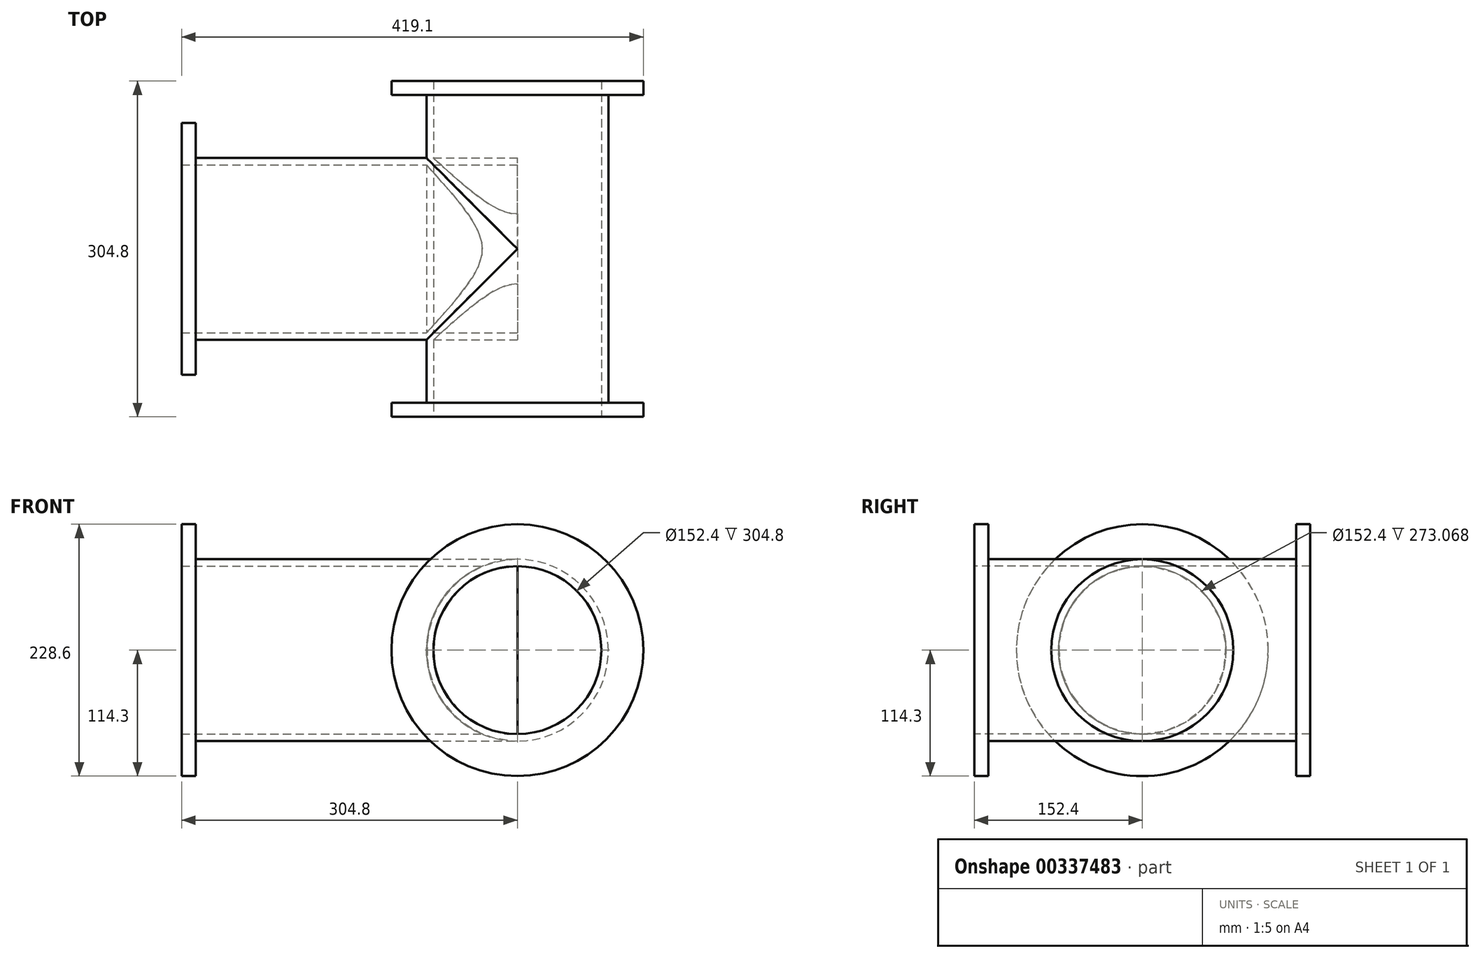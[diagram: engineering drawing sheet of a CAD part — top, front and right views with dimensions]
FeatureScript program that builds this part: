
annotation { "Feature Type Name" : "Feature", "Feature Type Description" : "" }
export const myFeature = defineFeature(function(context is Context, id is Id, definition is map)
    precondition{}
    {
        {
            var Q0;
            Q0=qCreatedBy(makeId("Right.planeOp"),FACE);
            var sketch = newSketch(context, id + "F0", { "sketchPlane" : qUnion([Q0])});
            skLineSegment(sketch, "E0", {"start": v(-372.41, 0) * mm, "end": v(512.39, 0) * mm, "construction": true});
            skLineSegment(sketch, "E1", {"start": v(0, 114.3) * mm, "end": v(-12.7, 114.3) * mm});
            skLineSegment(sketch, "E2", {"start": v(-12.7, 114.3) * mm, "end": v(-12.7, 82.55) * mm});
            skLineSegment(sketch, "E3", {"start": v(-12.7, 82.55) * mm, "end": v(-292.1, 82.55) * mm});
            skLineSegment(sketch, "E4", {"start": v(-292.1, 82.55) * mm, "end": v(-292.1, 114.3) * mm});
            skLineSegment(sketch, "E5", {"start": v(-292.1, 114.3) * mm, "end": v(-304.8, 114.3) * mm});
            skLineSegment(sketch, "E6", {"start": v(-304.8, 76.2) * mm, "end": v(0, 76.2) * mm});
            skLineSegment(sketch, "E7", {"start": v(-304.8, 114.3) * mm, "end": v(-304.8, 76.2) * mm});
            skLineSegment(sketch, "E8", {"start": v(0, 114.3) * mm, "end": v(0, 76.2) * mm});
            skSolve(sketch);
        }
        {
            var Q0;
            Q0=makeQuery(id+"F0.imprint","IMPRINT",FACE,{"disambiguationData":[TD([[makeQuery(id+"F0.imprint","IMPRINT",EDGE,{"derivedFrom":sQuery(id+"F0.wireOp",EDGE,"E1")}),1.0]])]});
            var Q1;
            Q1=sQuery(id+"F0.wireOp",EDGE,"E0");
            revolve(context, id + "F1", {"entities" : qUnion([Q0]), "axis" : qUnion([Q1]), "revolveType" : RevolveType.FULL});
        }
        {
            var Q0;
            Q0=makeQuery(id+"F1.opRevolve","SWEPT_FACE",FACE,{"disambiguationData":[OSD([sQuery(id+"F0.wireOp",EDGE,"E8")])]});
            var Q1;
            Q1=makeQuery(id+"F1.opRevolve","SWEPT_FACE",FACE,{"disambiguationData":[OSD([sQuery(id+"F0.wireOp",EDGE,"E7")])]});
            cPlane(context, id + "F2", {"entities" : qUnion([Q0, Q1]), "cplaneType" : CPlaneType.MID_PLANE, "offset" : 25.4 * mm, "width" : 152.4 * mm, "height" : 152.4 * mm});
        }
        {
            var Q0;
            Q0=qCreatedBy(id+"F2.planeOp",FACE);
            var sketch = newSketch(context, id + "F3", { "sketchPlane" : qUnion([Q0])});
            skLineSegment(sketch, "E9", {"start": v(304.8, 114.3) * mm, "end": v(292.1, 114.3) * mm});
            skLineSegment(sketch, "E10", {"start": v(292.1, 114.3) * mm, "end": v(292.1, 82.55) * mm});
            skLineSegment(sketch, "E11", {"start": v(292.1, 82.55) * mm, "end": v(0, 82.55) * mm});
            skLineSegment(sketch, "E12", {"start": v(0, 76.2) * mm, "end": v(304.8, 76.2) * mm});
            skLineSegment(sketch, "E13", {"start": v(304.8, 114.3) * mm, "end": v(304.8, 76.2) * mm});
            skLineSegment(sketch, "E14", {"start": v(0, 82.55) * mm, "end": v(0, 76.2) * mm});
            skLineSegment(sketch, "E15", {"start": v(328.87, 0) * mm, "end": v(-308.32, 0) * mm, "construction": true});
            skSolve(sketch);
        }
        {
            var Q0;
            Q0=makeQuery(id+"F3.imprint","IMPRINT",FACE,{"disambiguationData":[TD([[makeQuery(id+"F3.imprint","IMPRINT",EDGE,{"derivedFrom":sQuery(id+"F3.wireOp",EDGE,"E9")}),1.0]])]});
            var Q1;
            Q1=sQuery(id+"F3.wireOp",EDGE,"E15");
            revolve(context, id + "F4", {"operationType" : NewBodyOperationType.ADD, "entities" : qUnion([Q0]), "axis" : qUnion([Q1]), "revolveType" : RevolveType.FULL, "oppositeDirection" : true});
        }
    });
